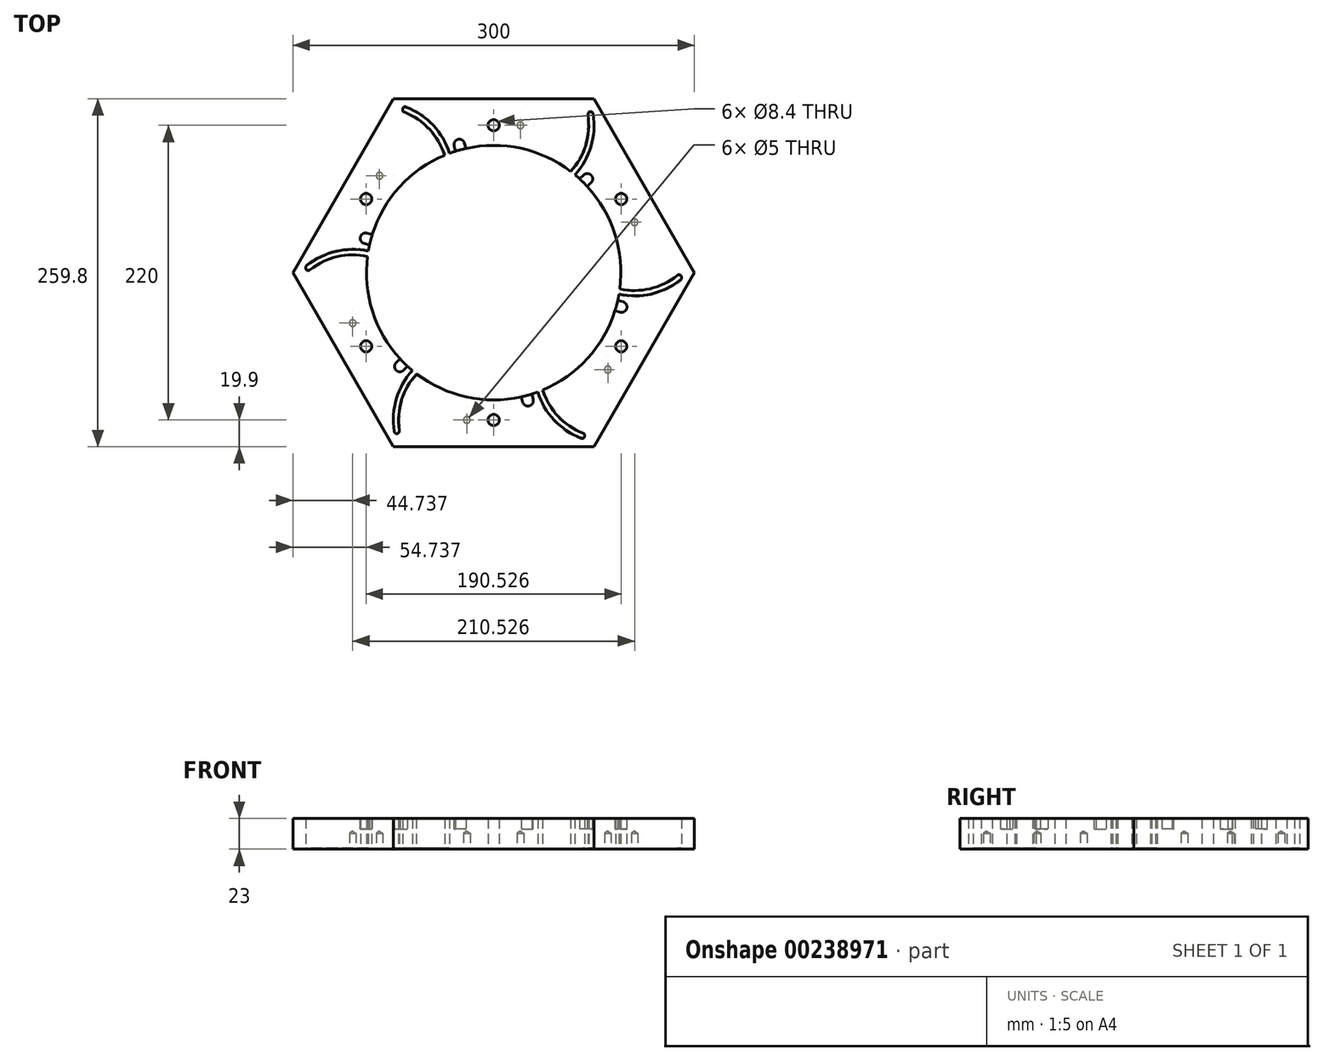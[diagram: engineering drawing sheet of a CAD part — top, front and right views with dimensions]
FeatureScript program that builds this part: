
annotation { "Feature Type Name" : "Feature", "Feature Type Description" : "" }
export const myFeature = defineFeature(function(context is Context, id is Id, definition is map)
    precondition{}
    {
        {
            var Q0;
            Q0=qCreatedBy(makeId("Top.planeOp"),FACE);
            var sketch = newSketch(context, id + "F0", { "sketchPlane" : qUnion([Q0])});
            skCircle(sketch, "E0.cCircle", {"center": v(0, 0) * mm, "radius": 150 * mm, "construction": true});
            skLineSegment(sketch, "E0.0", {"start": v(-75, 129.9) * mm, "end": v(75, 129.9) * mm});
            skLineSegment(sketch, "E0.1", {"start": v(75, 129.9) * mm, "end": v(150, 0) * mm});
            skLineSegment(sketch, "E0.2", {"start": v(150, 0) * mm, "end": v(75, -129.9) * mm});
            skLineSegment(sketch, "E0.3", {"start": v(75, -129.9) * mm, "end": v(-75, -129.9) * mm});
            skLineSegment(sketch, "E0.4", {"start": v(-75, -129.9) * mm, "end": v(-150, 0) * mm});
            skLineSegment(sketch, "E0.5", {"start": v(-150, 0) * mm, "end": v(-75, 129.9) * mm});
            skCircle(sketch, "E1", {"center": v(0, 0) * mm, "radius": 95 * mm});
            skCircle(sketch, "E2", {"center": v(0, 0) * mm, "radius": 110 * mm, "construction": true});
            skCircle(sketch, "E3", {"center": v(0, 110) * mm, "radius": 4.2 * mm});
            skCircle(sketch, "E4.1.0", {"center": v(-95.26, 55) * mm, "radius": 4.2 * mm});
            skCircle(sketch, "E4.2.0", {"center": v(-95.26, -55) * mm, "radius": 4.2 * mm});
            skCircle(sketch, "E4.3.0", {"center": v(0, -110) * mm, "radius": 4.2 * mm});
            skCircle(sketch, "E4.4.0", {"center": v(95.26, -55) * mm, "radius": 4.2 * mm});
            skCircle(sketch, "E4.5.0", {"center": v(95.26, 55) * mm, "radius": 4.2 * mm});
            skSolve(sketch);
        }
        {
            var Q0;
            Q0=qCreatedBy(makeId("Front.planeOp"),FACE);
            var sketch = newSketch(context, id + "F1", { "sketchPlane" : qUnion([Q0])});
            skLineSegment(sketch, "E5", {"start": v(0, -93.36) * mm, "end": v(0, 93) * mm, "construction": true});
            skSolve(sketch);
        }
        {
            var Q0;
            Q0=makeQuery(id+"F0.imprint","IMPRINT",FACE,{"disambiguationData":[TD([[makeQuery(id+"F0.imprint","IMPRINT",EDGE,{"derivedFrom":sQuery(id+"F0.wireOp",EDGE,"E0.0")}),-1.0]])]});
            extrude(context, id + "F2", {"entities" : qUnion([Q0]), "depth" : 25 * mm, "hasSecondDirection" : true, "secondDirectionOppositeDirection" : false, "secondDirectionDepth" : 2 * mm});
        }
        {
            var Q0;
            Q0=qCreatedBy(makeId("Top.planeOp"),FACE);
            var sketch = newSketch(context, id + "F3", { "sketchPlane" : qUnion([Q0])});
            skArc(sketch, "E6.0", {"start": v(-30.7, 79.26) * mm, "mid": v(-41.9, 106.16) * mm, "end": v(-65.27, 123.56) * mm});
            skArc(sketch, "E7.0", {"start": v(-34.54, 77.66) * mm, "mid": v(-44.72, 103.26) * mm, "end": v(-66.72, 119.83) * mm});
            skArc(sketch, "E8.0", {"start": v(-67.73, 122.7) * mm, "mid": v(-67.88, 121.03) * mm, "end": v(-66.72, 119.83) * mm});
            skArc(sketch, "E9.0", {"start": v(-65.27, 123.56) * mm, "mid": v(-66.66, 123.58) * mm, "end": v(-67.73, 122.7) * mm});
            skArc(sketch, "E10.0", {"start": v(-30.7, 79.26) * mm, "mid": v(-32.63, 78.49) * mm, "end": v(-34.54, 77.66) * mm});
            skSolve(sketch);
        }
        {
            var Q0;
            Q0=qSketchRegion(id+"F3",true);
            extrude(context, id + "F4", {"entities" : qUnion([Q0]), "depth" : 35 * mm, "hasSecondDirection" : true, "secondDirectionOppositeDirection" : true, "secondDirectionDepth" : 10 * mm});
        }
        {
            var Q0;
            Q0=makeQuery(id+"F4.opExtrude","SWEPT_BODY",BODY,{"disambiguationData":[OSD([sQuery(id+"F3.wireOp",EDGE,"E6.0"),sQuery(id+"F3.wireOp",EDGE,"E7.0"),sQuery(id+"F3.wireOp",EDGE,"E8.0"),sQuery(id+"F3.wireOp",EDGE,"E9.0"),sQuery(id+"F3.wireOp",EDGE,"E10.0")])]});
            var Q1;
            Q1=sQuery(id+"F1.wireOp",EDGE,"E5");
            circularPattern(context, id + "F5", {"entities" : qUnion([Q0]), "axis" : qUnion([Q1]), "angle" : 360 * degree, "instanceCount" : 6, "equalSpace" : true});
        }
        {
            var Q0;
            Q0=makeQuery(id+"F4.opExtrude","SWEPT_BODY",BODY,{"disambiguationData":[OSD([sQuery(id+"F3.wireOp",EDGE,"E6.0"),sQuery(id+"F3.wireOp",EDGE,"E7.0"),sQuery(id+"F3.wireOp",EDGE,"E8.0"),sQuery(id+"F3.wireOp",EDGE,"E9.0"),sQuery(id+"F3.wireOp",EDGE,"E10.0")])]});
            var Q1;
            Q1=makeQuery(id+"F5.opPattern","COPY",BODY,{"derivedFrom":makeQuery(id+"F4.opExtrude","SWEPT_BODY",BODY,{"disambiguationData":[OSD([sQuery(id+"F3.wireOp",EDGE,"E6.0"),sQuery(id+"F3.wireOp",EDGE,"E7.0"),sQuery(id+"F3.wireOp",EDGE,"E8.0"),sQuery(id+"F3.wireOp",EDGE,"E9.0"),sQuery(id+"F3.wireOp",EDGE,"E10.0")])]}),"instanceName":"5"});
            var Q2;
            Q2=makeQuery(id+"F5.opPattern","COPY",BODY,{"derivedFrom":makeQuery(id+"F4.opExtrude","SWEPT_BODY",BODY,{"disambiguationData":[OSD([sQuery(id+"F3.wireOp",EDGE,"E6.0"),sQuery(id+"F3.wireOp",EDGE,"E7.0"),sQuery(id+"F3.wireOp",EDGE,"E8.0"),sQuery(id+"F3.wireOp",EDGE,"E9.0"),sQuery(id+"F3.wireOp",EDGE,"E10.0")])]}),"instanceName":"4"});
            var Q3;
            Q3=makeQuery(id+"F5.opPattern","COPY",BODY,{"derivedFrom":makeQuery(id+"F4.opExtrude","SWEPT_BODY",BODY,{"disambiguationData":[OSD([sQuery(id+"F3.wireOp",EDGE,"E6.0"),sQuery(id+"F3.wireOp",EDGE,"E7.0"),sQuery(id+"F3.wireOp",EDGE,"E8.0"),sQuery(id+"F3.wireOp",EDGE,"E9.0"),sQuery(id+"F3.wireOp",EDGE,"E10.0")])]}),"instanceName":"3"});
            var Q4;
            Q4=makeQuery(id+"F5.opPattern","COPY",BODY,{"derivedFrom":makeQuery(id+"F4.opExtrude","SWEPT_BODY",BODY,{"disambiguationData":[OSD([sQuery(id+"F3.wireOp",EDGE,"E6.0"),sQuery(id+"F3.wireOp",EDGE,"E7.0"),sQuery(id+"F3.wireOp",EDGE,"E8.0"),sQuery(id+"F3.wireOp",EDGE,"E9.0"),sQuery(id+"F3.wireOp",EDGE,"E10.0")])]}),"instanceName":"2"});
            var Q5;
            Q5=makeQuery(id+"F5.opPattern","COPY",BODY,{"derivedFrom":makeQuery(id+"F4.opExtrude","SWEPT_BODY",BODY,{"disambiguationData":[OSD([sQuery(id+"F3.wireOp",EDGE,"E6.0"),sQuery(id+"F3.wireOp",EDGE,"E7.0"),sQuery(id+"F3.wireOp",EDGE,"E8.0"),sQuery(id+"F3.wireOp",EDGE,"E9.0"),sQuery(id+"F3.wireOp",EDGE,"E10.0")])]}),"instanceName":"1"});
            var Q6;
            Q6=makeQuery(id+"F2.opExtrude","SWEPT_BODY",BODY,{"disambiguationData":[OSD([sQuery(id+"F0.wireOp",EDGE,"E0.0"),sQuery(id+"F0.wireOp",EDGE,"E0.1"),sQuery(id+"F0.wireOp",EDGE,"E0.2"),sQuery(id+"F0.wireOp",EDGE,"E0.3"),sQuery(id+"F0.wireOp",EDGE,"E0.4"),sQuery(id+"F0.wireOp",EDGE,"E0.5"),sQuery(id+"F0.wireOp",EDGE,"E1")])]});
            booleanBodies(context, id + "F6", {"operationType" : BooleanOperationType.SUBTRACTION, "tools" : qUnion([Q0, Q1, Q2, Q3, Q4, Q5]), "targets" : qUnion([Q6])});
        }
        {
            var Q0;
            Q0=makeQuery(id+"F2.opExtrude","CAP_FACE",FACE,{"disambiguationData":[OSD([sQuery(id+"F0.wireOp",EDGE,"E0.0"),sQuery(id+"F0.wireOp",EDGE,"E0.1"),sQuery(id+"F0.wireOp",EDGE,"E0.2"),sQuery(id+"F0.wireOp",EDGE,"E0.3"),sQuery(id+"F0.wireOp",EDGE,"E0.4"),sQuery(id+"F0.wireOp",EDGE,"E0.5"),sQuery(id+"F0.wireOp",EDGE,"E1")])],"isStart":false});
            var sketch = newSketch(context, id + "F7", { "sketchPlane" : qUnion([Q0])});
            skCircle(sketch, "E11", {"center": v(0, 0) * mm, "radius": 95 * mm, "construction": true});
            skCircle(sketch, "E12", {"center": v(0, 0) * mm, "radius": 99 * mm, "construction": true});
            skLineSegment(sketch, "E13", {"start": v(0, 0) * mm, "end": v(0, 115.62) * mm, "construction": true});
            skLineSegment(sketch, "E14", {"start": v(0, 0) * mm, "end": v(-31.28, 116.73) * mm, "construction": true});
            skPoint(sketch, "E15", {"position": v(-25.62, 95.63) * mm});
            skArc(sketch, "E16", {"start": v(-26.66, 99.5) * mm, "mid": v(-29.1, 97.6) * mm, "end": v(-29.47, 94.51) * mm});
            skLineSegment(sketch, "E17", {"start": v(-29.49, 94.6) * mm, "end": v(-26.61, 83.86) * mm});
            skLineSegment(sketch, "E18", {"start": v(-22.75, 84.9) * mm, "end": v(-26.61, 83.86) * mm});
            skArc(sketch, "E19.MirrorCS", {"start": v(-26.66, 99.5) * mm, "mid": v(-23.59, 99.07) * mm, "end": v(-21.74, 96.58) * mm});
            skLineSegment(sketch, "E20.MirrorCS", {"start": v(-22.75, 84.9) * mm, "end": v(-18.88, 85.93) * mm});
            skLineSegment(sketch, "E21.MirrorCS", {"start": v(-21.76, 96.66) * mm, "end": v(-18.88, 85.93) * mm});
            skPoint(sketch, "E22", {"position": v(-32.9, 89.12) * mm});
            skPoint(sketch, "E23", {"position": v(-24.59, 91.76) * mm});
            skLineSegment(sketch, "E24", {"start": v(0, 0) * mm, "end": v(51.23, 96.35) * mm, "construction": true});
            skPoint(sketch, "E25", {"position": v(57.6, 75.55) * mm});
            skPoint(sketch, "E26", {"position": v(44.6, 83.88) * mm});
            skPoint(sketch, "E27", {"position": v(46.48, 87.41) * mm});
            skArc(sketch, "E28", {"start": v(48.36, 90.94) * mm, "mid": v(45.3, 91.24) * mm, "end": v(42.95, 89.29) * mm, "construction": true});
            skLineSegment(sketch, "E29", {"start": v(42.95, 89.29) * mm, "end": v(41.03, 85.68) * mm, "construction": true});
            skArc(sketch, "E30.MirrorCS", {"start": v(48.36, 90.94) * mm, "mid": v(50.3, 88.58) * mm, "end": v(50, 85.53) * mm, "construction": true});
            skLineSegment(sketch, "E31.MirrorCS", {"start": v(50, 85.53) * mm, "end": v(48.1, 81.93) * mm, "construction": true});
            skSolve(sketch);
        }
        {
            var Q0;
            Q0=qSketchRegion(id+"F7",true);
            extrude(context, id + "F8", {"entities" : qUnion([Q0]), "oppositeDirection" : true, "depth" : 8 * mm, "hasSecondDirection" : true, "secondDirectionOppositeDirection" : false, "secondDirectionDepth" : 10 * mm});
        }
        {
            var Q0;
            Q0=makeQuery(id+"F8.opExtrude","SWEPT_BODY",BODY,{"disambiguationData":[OSD([sQuery(id+"F7.wireOp",EDGE,"E16"),sQuery(id+"F7.wireOp",EDGE,"E17"),sQuery(id+"F7.wireOp",EDGE,"E18"),sQuery(id+"F7.wireOp",EDGE,"E19.MirrorCS"),sQuery(id+"F7.wireOp",EDGE,"E20.MirrorCS"),sQuery(id+"F7.wireOp",EDGE,"E21.MirrorCS")])]});
            var Q1;
            Q1=sQuery(id+"F1.wireOp",EDGE,"E5");
            circularPattern(context, id + "F9", {"operationType" : NewBodyOperationType.REMOVE, "entities" : qUnion([Q0]), "axis" : qUnion([Q1]), "angle" : 360 * degree, "instanceCount" : 6, "equalSpace" : true});
        }
        {
            var Q0;
            Q0=makeQuery(id+"F0.imprint","IMPRINT",FACE,{"disambiguationData":[TD([[makeQuery(id+"F0.imprint","IMPRINT",EDGE,{"derivedFrom":sQuery(id+"F0.wireOp",EDGE,"E0.0")}),-1.0]])]});
            cPlane(context, id + "F10", {"entities" : qUnion([Q0]), "cplaneType" : CPlaneType.OFFSET, "offset" : 0 * mm, "width" : 150 * mm, "height" : 150 * mm});
        }
        {
            var Q0;
            Q0=qCreatedBy(id+"F10.planeOp",FACE);
            var sketch = newSketch(context, id + "F11", { "sketchPlane" : qUnion([Q0])});
            skPoint(sketch, "E32.0", {"position": v(-85.26, 72.32) * mm});
            skPoint(sketch, "E33.1.0", {"position": v(-105.26, -37.68) * mm});
            skPoint(sketch, "E33.2.0", {"position": v(-20, -110) * mm});
            skPoint(sketch, "E33.3.0", {"position": v(85.26, -72.32) * mm});
            skPoint(sketch, "E33.4.0", {"position": v(105.26, 37.68) * mm});
            skPoint(sketch, "E33.5.0", {"position": v(20, 110) * mm});
            skPoint(sketch, "E33.center", {"position": v(0, 0) * mm});
            skSolve(sketch);
        }
        {
            var Q0;
            Q0=sQuery(id+"F11.wireOp",VERTEX,"E32.0");
            var Q1;
            Q1=sQuery(id+"F11.wireOp",VERTEX,"E33.5.0");
            var Q2;
            Q2=sQuery(id+"F11.wireOp",VERTEX,"E33.4.0");
            var Q3;
            Q3=sQuery(id+"F11.wireOp",VERTEX,"E33.3.0");
            var Q4;
            Q4=sQuery(id+"F11.wireOp",VERTEX,"E33.2.0");
            var Q5;
            Q5=sQuery(id+"F11.wireOp",VERTEX,"E33.1.0");
            var Q6;
            Q6=makeQuery(id+"F2.opExtrude","SWEPT_BODY",BODY,{"disambiguationData":[OSD([sQuery(id+"F0.wireOp",EDGE,"E0.0"),sQuery(id+"F0.wireOp",EDGE,"E0.1"),sQuery(id+"F0.wireOp",EDGE,"E0.2"),sQuery(id+"F0.wireOp",EDGE,"E0.3"),sQuery(id+"F0.wireOp",EDGE,"E0.4"),sQuery(id+"F0.wireOp",EDGE,"E0.5"),sQuery(id+"F0.wireOp",EDGE,"E1"),sQuery(id+"F0.wireOp",EDGE,"E3"),sQuery(id+"F0.wireOp",EDGE,"E4.1.0"),sQuery(id+"F0.wireOp",EDGE,"E4.2.0"),sQuery(id+"F0.wireOp",EDGE,"E4.3.0"),sQuery(id+"F0.wireOp",EDGE,"E4.4.0"),sQuery(id+"F0.wireOp",EDGE,"E4.5.0")])]});
            hole(context, id + "F12", {"style" : HoleStyle.SIMPLE, "endStyle" : HoleEndStyle.BLIND, "oppositeDirection" : true, "holeDiameter" : 5 * mm, "holeDepth" : 12 * mm, "locations" : qUnion([Q0, Q1, Q2, Q3, Q4, Q5]), "scope" : qUnion([Q6])});
        }
        {
            var Q0;
            Q0=makeQuery(id+"F6.opBoolean","INTERSECT",EDGE,{"derivedFrom":[makeQuery(id+"F2.opExtrude","CAP_FACE",FACE,{"disambiguationData":[OSD([sQuery(id+"F0.wireOp",EDGE,"E0.0"),sQuery(id+"F0.wireOp",EDGE,"E0.1"),sQuery(id+"F0.wireOp",EDGE,"E0.2"),sQuery(id+"F0.wireOp",EDGE,"E0.3"),sQuery(id+"F0.wireOp",EDGE,"E0.4"),sQuery(id+"F0.wireOp",EDGE,"E0.5"),sQuery(id+"F0.wireOp",EDGE,"E1"),sQuery(id+"F0.wireOp",EDGE,"E3"),sQuery(id+"F0.wireOp",EDGE,"E4.1.0"),sQuery(id+"F0.wireOp",EDGE,"E4.2.0"),sQuery(id+"F0.wireOp",EDGE,"E4.3.0"),sQuery(id+"F0.wireOp",EDGE,"E4.4.0"),sQuery(id+"F0.wireOp",EDGE,"E4.5.0")])],"isStart":true}),makeQuery(id+"F5.opPattern","COPY",FACE,{"derivedFrom":makeQuery(id+"F4.opExtrude","SWEPT_FACE",FACE,{"disambiguationData":[OSD([sQuery(id+"F3.wireOp",EDGE,"E7.0")])]}),"instanceName":"3"})]});
            var Q1;
            Q1=makeQuery(id+"F6.opBoolean","INTERSECT",EDGE,{"derivedFrom":[makeQuery(id+"F2.opExtrude","CAP_FACE",FACE,{"disambiguationData":[OSD([sQuery(id+"F0.wireOp",EDGE,"E0.0"),sQuery(id+"F0.wireOp",EDGE,"E0.1"),sQuery(id+"F0.wireOp",EDGE,"E0.2"),sQuery(id+"F0.wireOp",EDGE,"E0.3"),sQuery(id+"F0.wireOp",EDGE,"E0.4"),sQuery(id+"F0.wireOp",EDGE,"E0.5"),sQuery(id+"F0.wireOp",EDGE,"E1"),sQuery(id+"F0.wireOp",EDGE,"E3"),sQuery(id+"F0.wireOp",EDGE,"E4.1.0"),sQuery(id+"F0.wireOp",EDGE,"E4.2.0"),sQuery(id+"F0.wireOp",EDGE,"E4.3.0"),sQuery(id+"F0.wireOp",EDGE,"E4.4.0"),sQuery(id+"F0.wireOp",EDGE,"E4.5.0")])],"isStart":true}),makeQuery(id+"F5.opPattern","COPY",FACE,{"derivedFrom":makeQuery(id+"F4.opExtrude","SWEPT_FACE",FACE,{"disambiguationData":[OSD([sQuery(id+"F3.wireOp",EDGE,"E7.0")])]}),"instanceName":"4"})]});
            var Q2;
            Q2=makeQuery(id+"F6.opBoolean","INTERSECT",EDGE,{"derivedFrom":[makeQuery(id+"F2.opExtrude","CAP_FACE",FACE,{"disambiguationData":[OSD([sQuery(id+"F0.wireOp",EDGE,"E0.0"),sQuery(id+"F0.wireOp",EDGE,"E0.1"),sQuery(id+"F0.wireOp",EDGE,"E0.2"),sQuery(id+"F0.wireOp",EDGE,"E0.3"),sQuery(id+"F0.wireOp",EDGE,"E0.4"),sQuery(id+"F0.wireOp",EDGE,"E0.5"),sQuery(id+"F0.wireOp",EDGE,"E1"),sQuery(id+"F0.wireOp",EDGE,"E3"),sQuery(id+"F0.wireOp",EDGE,"E4.1.0"),sQuery(id+"F0.wireOp",EDGE,"E4.2.0"),sQuery(id+"F0.wireOp",EDGE,"E4.3.0"),sQuery(id+"F0.wireOp",EDGE,"E4.4.0"),sQuery(id+"F0.wireOp",EDGE,"E4.5.0")])],"isStart":true}),makeQuery(id+"F5.opPattern","COPY",FACE,{"derivedFrom":makeQuery(id+"F4.opExtrude","SWEPT_FACE",FACE,{"disambiguationData":[OSD([sQuery(id+"F3.wireOp",EDGE,"E7.0")])]}),"instanceName":"5"})]});
            var Q3;
            Q3=makeQuery(id+"F6.opBoolean","INTERSECT",EDGE,{"derivedFrom":[makeQuery(id+"F2.opExtrude","CAP_FACE",FACE,{"disambiguationData":[OSD([sQuery(id+"F0.wireOp",EDGE,"E0.0"),sQuery(id+"F0.wireOp",EDGE,"E0.1"),sQuery(id+"F0.wireOp",EDGE,"E0.2"),sQuery(id+"F0.wireOp",EDGE,"E0.3"),sQuery(id+"F0.wireOp",EDGE,"E0.4"),sQuery(id+"F0.wireOp",EDGE,"E0.5"),sQuery(id+"F0.wireOp",EDGE,"E1"),sQuery(id+"F0.wireOp",EDGE,"E3"),sQuery(id+"F0.wireOp",EDGE,"E4.1.0"),sQuery(id+"F0.wireOp",EDGE,"E4.2.0"),sQuery(id+"F0.wireOp",EDGE,"E4.3.0"),sQuery(id+"F0.wireOp",EDGE,"E4.4.0"),sQuery(id+"F0.wireOp",EDGE,"E4.5.0")])],"isStart":true}),makeQuery(id+"F4.opExtrude","SWEPT_FACE",FACE,{"disambiguationData":[OSD([sQuery(id+"F3.wireOp",EDGE,"E7.0")])]})]});
            var Q4;
            Q4=makeQuery(id+"F6.opBoolean","INTERSECT",EDGE,{"derivedFrom":[makeQuery(id+"F2.opExtrude","CAP_FACE",FACE,{"disambiguationData":[OSD([sQuery(id+"F0.wireOp",EDGE,"E0.0"),sQuery(id+"F0.wireOp",EDGE,"E0.1"),sQuery(id+"F0.wireOp",EDGE,"E0.2"),sQuery(id+"F0.wireOp",EDGE,"E0.3"),sQuery(id+"F0.wireOp",EDGE,"E0.4"),sQuery(id+"F0.wireOp",EDGE,"E0.5"),sQuery(id+"F0.wireOp",EDGE,"E1"),sQuery(id+"F0.wireOp",EDGE,"E3"),sQuery(id+"F0.wireOp",EDGE,"E4.1.0"),sQuery(id+"F0.wireOp",EDGE,"E4.2.0"),sQuery(id+"F0.wireOp",EDGE,"E4.3.0"),sQuery(id+"F0.wireOp",EDGE,"E4.4.0"),sQuery(id+"F0.wireOp",EDGE,"E4.5.0")])],"isStart":true}),makeQuery(id+"F5.opPattern","COPY",FACE,{"derivedFrom":makeQuery(id+"F4.opExtrude","SWEPT_FACE",FACE,{"disambiguationData":[OSD([sQuery(id+"F3.wireOp",EDGE,"E7.0")])]}),"instanceName":"1"})]});
            var Q5;
            Q5=makeQuery(id+"F6.opBoolean","INTERSECT",EDGE,{"derivedFrom":[makeQuery(id+"F2.opExtrude","CAP_FACE",FACE,{"disambiguationData":[OSD([sQuery(id+"F0.wireOp",EDGE,"E0.0"),sQuery(id+"F0.wireOp",EDGE,"E0.1"),sQuery(id+"F0.wireOp",EDGE,"E0.2"),sQuery(id+"F0.wireOp",EDGE,"E0.3"),sQuery(id+"F0.wireOp",EDGE,"E0.4"),sQuery(id+"F0.wireOp",EDGE,"E0.5"),sQuery(id+"F0.wireOp",EDGE,"E1"),sQuery(id+"F0.wireOp",EDGE,"E3"),sQuery(id+"F0.wireOp",EDGE,"E4.1.0"),sQuery(id+"F0.wireOp",EDGE,"E4.2.0"),sQuery(id+"F0.wireOp",EDGE,"E4.3.0"),sQuery(id+"F0.wireOp",EDGE,"E4.4.0"),sQuery(id+"F0.wireOp",EDGE,"E4.5.0")])],"isStart":true}),makeQuery(id+"F5.opPattern","COPY",FACE,{"derivedFrom":makeQuery(id+"F4.opExtrude","SWEPT_FACE",FACE,{"disambiguationData":[OSD([sQuery(id+"F3.wireOp",EDGE,"E7.0")])]}),"instanceName":"2"})]});
            chamfer(context, id + "F13", {"entities" : qUnion([Q0, Q1, Q2, Q3, Q4, Q5]), "width" : 0.6 * mm, "tangentPropagation" : true});
        }
        {
            var Q0;
            Q0=makeQuery(id+"F2.opExtrude","CAP_FACE",FACE,{"disambiguationData":[OSD([sQuery(id+"F0.wireOp",EDGE,"E0.0"),sQuery(id+"F0.wireOp",EDGE,"E0.1"),sQuery(id+"F0.wireOp",EDGE,"E0.2"),sQuery(id+"F0.wireOp",EDGE,"E0.3"),sQuery(id+"F0.wireOp",EDGE,"E0.4"),sQuery(id+"F0.wireOp",EDGE,"E0.5"),sQuery(id+"F0.wireOp",EDGE,"E1"),sQuery(id+"F0.wireOp",EDGE,"E3"),sQuery(id+"F0.wireOp",EDGE,"E4.1.0"),sQuery(id+"F0.wireOp",EDGE,"E4.2.0"),sQuery(id+"F0.wireOp",EDGE,"E4.3.0"),sQuery(id+"F0.wireOp",EDGE,"E4.4.0"),sQuery(id+"F0.wireOp",EDGE,"E4.5.0")])],"isStart":false});
            cPlane(context, id + "F14", {"entities" : qUnion([Q0]), "cplaneType" : CPlaneType.OFFSET, "offset" : 25 * mm, "width" : 150 * mm, "height" : 150 * mm});
        }
    });
